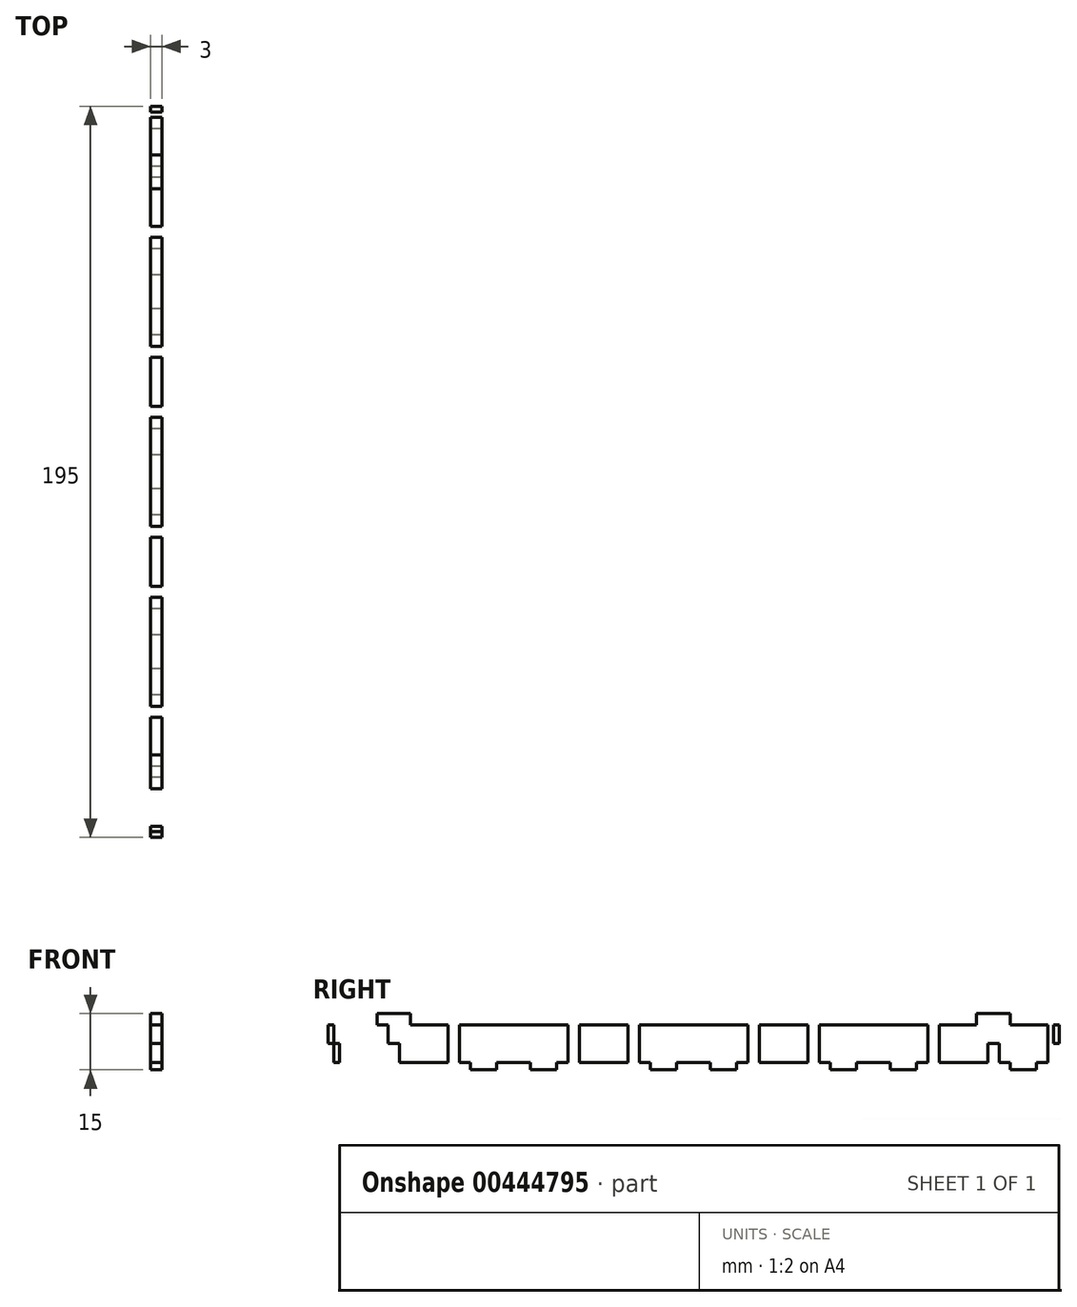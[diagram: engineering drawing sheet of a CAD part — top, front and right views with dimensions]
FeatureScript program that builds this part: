
annotation { "Feature Type Name" : "Feature", "Feature Type Description" : "" }
export const myFeature = defineFeature(function(context is Context, id is Id, definition is map)
    precondition{}
    {
        {
            var Q0;
            Q0=qCreatedBy(makeId("Right.planeOp"),FACE);
            var sketch = newSketch(context, id + "F0", { "sketchPlane" : qUnion([Q0])});
            skLineSegment(sketch, "E0", {"start": v(0, 0) * mm, "end": v(4.5, 0) * mm});
            skLineSegment(sketch, "E1", {"start": v(4.5, 0) * mm, "end": v(4.5, -2) * mm});
            skLineSegment(sketch, "E2", {"start": v(4.5, -2) * mm, "end": v(11.5, -2) * mm});
            skLineSegment(sketch, "E3", {"start": v(11.5, -2) * mm, "end": v(11.5, 0) * mm});
            skLineSegment(sketch, "E4", {"start": v(11.5, 0) * mm, "end": v(36.5, 0) * mm});
            skLineSegment(sketch, "E5", {"start": v(36.5, 0) * mm, "end": v(36.5, -2) * mm});
            skLineSegment(sketch, "E6", {"start": v(36.5, -2) * mm, "end": v(43.5, -2) * mm});
            skLineSegment(sketch, "E7", {"start": v(43.5, -2) * mm, "end": v(43.5, 0) * mm});
            skLineSegment(sketch, "E8", {"start": v(43.5, 0) * mm, "end": v(48, 0) * mm});
            skLineSegment(sketch, "E9.1.0.0", {"start": v(52.5, -2) * mm, "end": v(59.5, -2) * mm});
            skLineSegment(sketch, "E9.1.0.1", {"start": v(59.5, 0) * mm, "end": v(84.5, 0) * mm});
            skLineSegment(sketch, "E9.1.0.2", {"start": v(84.5, -2) * mm, "end": v(91.5, -2) * mm});
            skLineSegment(sketch, "E9.1.0.3", {"start": v(91.5, 0) * mm, "end": v(96, 0) * mm});
            skLineSegment(sketch, "E9.1.0.4", {"start": v(48, 0) * mm, "end": v(52.5, 0) * mm});
            skLineSegment(sketch, "E9.1.0.5", {"start": v(52.5, 0) * mm, "end": v(52.5, -2) * mm});
            skLineSegment(sketch, "E9.1.0.6", {"start": v(91.5, -2) * mm, "end": v(91.5, 0) * mm});
            skLineSegment(sketch, "E9.1.0.7", {"start": v(59.5, -2) * mm, "end": v(59.5, 0) * mm});
            skLineSegment(sketch, "E9.1.0.8", {"start": v(84.5, 0) * mm, "end": v(84.5, -2) * mm});
            skLineSegment(sketch, "E9.2.0.0", {"start": v(100.5, -2) * mm, "end": v(107.5, -2) * mm});
            skLineSegment(sketch, "E9.2.0.1", {"start": v(107.5, 0) * mm, "end": v(132.5, 0) * mm});
            skLineSegment(sketch, "E9.2.0.2", {"start": v(132.5, -2) * mm, "end": v(139.5, -2) * mm});
            skLineSegment(sketch, "E9.2.0.3", {"start": v(139.5, 0) * mm, "end": v(144, 0) * mm});
            skLineSegment(sketch, "E9.2.0.4", {"start": v(96, 0) * mm, "end": v(100.5, 0) * mm});
            skLineSegment(sketch, "E9.2.0.5", {"start": v(100.5, 0) * mm, "end": v(100.5, -2) * mm});
            skLineSegment(sketch, "E9.2.0.6", {"start": v(139.5, -2) * mm, "end": v(139.5, 0) * mm});
            skLineSegment(sketch, "E9.2.0.7", {"start": v(107.5, -2) * mm, "end": v(107.5, 0) * mm});
            skLineSegment(sketch, "E9.2.0.8", {"start": v(132.5, 0) * mm, "end": v(132.5, -2) * mm});
            skLineSegment(sketch, "E9.3.0.0", {"start": v(148.5, -2) * mm, "end": v(155.5, -2) * mm});
            skLineSegment(sketch, "E9.3.0.1", {"start": v(155.5, 0) * mm, "end": v(180.5, 0) * mm});
            skLineSegment(sketch, "E9.3.0.2", {"start": v(180.5, -2) * mm, "end": v(187.5, -2) * mm});
            skLineSegment(sketch, "E9.3.0.3", {"start": v(187.5, 0) * mm, "end": v(192, 0) * mm});
            skLineSegment(sketch, "E9.3.0.4", {"start": v(144, 0) * mm, "end": v(148.5, 0) * mm});
            skLineSegment(sketch, "E9.3.0.5", {"start": v(148.5, 0) * mm, "end": v(148.5, -2) * mm});
            skLineSegment(sketch, "E9.3.0.6", {"start": v(187.5, -2) * mm, "end": v(187.5, 0) * mm});
            skLineSegment(sketch, "E9.3.0.7", {"start": v(155.5, -2) * mm, "end": v(155.5, 0) * mm});
            skLineSegment(sketch, "E9.3.0.8", {"start": v(180.5, 0) * mm, "end": v(180.5, -2) * mm});
            skLineSegment(sketch, "E9.direction1", {"start": v(0, 0) * mm, "end": v(48, 0) * mm, "construction": true});
            skLineSegment(sketch, "E10", {"start": v(0, 0) * mm, "end": v(0, 10) * mm});
            skLineSegment(sketch, "E11", {"start": v(192, 0) * mm, "end": v(192, 10) * mm});
            skLineSegment(sketch, "E12", {"start": v(192, 10) * mm, "end": v(0, 10) * mm});
            skPoint(sketch, "E13.oppositeSnap0", {"position": v(0, 5) * mm});
            skLineSegment(sketch, "E13.bottom", {"start": v(0, 10) * mm, "end": v(-1.5, 10) * mm});
            skLineSegment(sketch, "E13.top", {"start": v(0, 5) * mm, "end": v(-1.5, 5) * mm});
            skLineSegment(sketch, "E13.left", {"start": v(0, 10) * mm, "end": v(0, 5) * mm});
            skLineSegment(sketch, "E13.right", {"start": v(-1.5, 10) * mm, "end": v(-1.5, 5) * mm});
            skPoint(sketch, "E14.oppositeSnap0", {"position": v(192, 5) * mm});
            skLineSegment(sketch, "E14.bottom", {"start": v(192, 10) * mm, "end": v(193.5, 10) * mm});
            skLineSegment(sketch, "E14.top", {"start": v(192, 5) * mm, "end": v(193.5, 5) * mm});
            skLineSegment(sketch, "E14.left", {"start": v(192, 10) * mm, "end": v(192, 5) * mm});
            skLineSegment(sketch, "E14.right", {"start": v(193.5, 10) * mm, "end": v(193.5, 5) * mm});
            skLineSegment(sketch, "E15.bottom", {"start": v(14.5, 10) * mm, "end": v(17.5, 10) * mm});
            skLineSegment(sketch, "E15.top", {"start": v(14.5, 5) * mm, "end": v(17.5, 5) * mm});
            skLineSegment(sketch, "E15.left", {"start": v(14.5, 10) * mm, "end": v(14.5, 5) * mm});
            skLineSegment(sketch, "E15.right", {"start": v(17.5, 10) * mm, "end": v(17.5, 5) * mm});
            skLineSegment(sketch, "E16.bottom", {"start": v(33.5, 10) * mm, "end": v(30.5, 10) * mm});
            skLineSegment(sketch, "E16.top", {"start": v(33.5, 5) * mm, "end": v(30.5, 5) * mm});
            skLineSegment(sketch, "E16.left", {"start": v(33.5, 10) * mm, "end": v(33.5, 5) * mm});
            skLineSegment(sketch, "E16.right", {"start": v(30.5, 10) * mm, "end": v(30.5, 5) * mm});
            skLineSegment(sketch, "E17.bottom", {"start": v(62.5, 10) * mm, "end": v(65.5, 10) * mm});
            skLineSegment(sketch, "E17.top", {"start": v(62.5, 5) * mm, "end": v(65.5, 5) * mm});
            skLineSegment(sketch, "E17.left", {"start": v(62.5, 10) * mm, "end": v(62.5, 5) * mm});
            skLineSegment(sketch, "E17.right", {"start": v(65.5, 10) * mm, "end": v(65.5, 5) * mm});
            skLineSegment(sketch, "E18.bottom", {"start": v(78.5, 10) * mm, "end": v(81.5, 10) * mm});
            skLineSegment(sketch, "E18.top", {"start": v(78.5, 5) * mm, "end": v(81.5, 5) * mm});
            skLineSegment(sketch, "E18.left", {"start": v(78.5, 10) * mm, "end": v(78.5, 5) * mm});
            skLineSegment(sketch, "E18.right", {"start": v(81.5, 10) * mm, "end": v(81.5, 5) * mm});
            skLineSegment(sketch, "E19.bottom", {"start": v(110.5, 10) * mm, "end": v(113.5, 10) * mm});
            skLineSegment(sketch, "E19.top", {"start": v(110.5, 5) * mm, "end": v(113.5, 5) * mm});
            skLineSegment(sketch, "E19.left", {"start": v(110.5, 10) * mm, "end": v(110.5, 5) * mm});
            skLineSegment(sketch, "E19.right", {"start": v(113.5, 10) * mm, "end": v(113.5, 5) * mm});
            skLineSegment(sketch, "E20.bottom", {"start": v(129.5, 10) * mm, "end": v(126.5, 10) * mm});
            skLineSegment(sketch, "E20.top", {"start": v(129.5, 5) * mm, "end": v(126.5, 5) * mm});
            skLineSegment(sketch, "E20.left", {"start": v(129.5, 10) * mm, "end": v(129.5, 5) * mm});
            skLineSegment(sketch, "E20.right", {"start": v(126.5, 10) * mm, "end": v(126.5, 5) * mm});
            skLineSegment(sketch, "E21.bottom", {"start": v(158.5, 10) * mm, "end": v(161.5, 10) * mm});
            skLineSegment(sketch, "E21.top", {"start": v(158.5, 5) * mm, "end": v(161.5, 5) * mm});
            skLineSegment(sketch, "E21.left", {"start": v(158.5, 10) * mm, "end": v(158.5, 5) * mm});
            skLineSegment(sketch, "E21.right", {"start": v(161.5, 10) * mm, "end": v(161.5, 5) * mm});
            skLineSegment(sketch, "E22.bottom", {"start": v(177.5, 10) * mm, "end": v(174.5, 10) * mm});
            skLineSegment(sketch, "E22.top", {"start": v(177.5, 5) * mm, "end": v(174.5, 5) * mm});
            skLineSegment(sketch, "E22.left", {"start": v(177.5, 10) * mm, "end": v(177.5, 5) * mm});
            skLineSegment(sketch, "E22.right", {"start": v(174.5, 10) * mm, "end": v(174.5, 5) * mm});
            skLineSegment(sketch, "E23.top", {"start": v(0, 0) * mm, "end": v(-1.5, 0) * mm});
            skLineSegment(sketch, "E23.left", {"start": v(0, 5) * mm, "end": v(0, 0) * mm});
            skLineSegment(sketch, "E23.right", {"start": v(-1.5, 5) * mm, "end": v(-1.5, 0) * mm});
            skLineSegment(sketch, "E24.top", {"start": v(14.5, 0) * mm, "end": v(17.5, 0) * mm});
            skLineSegment(sketch, "E24.left", {"start": v(14.5, 5) * mm, "end": v(14.5, 0) * mm});
            skLineSegment(sketch, "E24.right", {"start": v(17.5, 5) * mm, "end": v(17.5, 0) * mm});
            skLineSegment(sketch, "E25.bottom", {"start": v(30.5, 5) * mm, "end": v(33.5, 5) * mm});
            skLineSegment(sketch, "E25.top", {"start": v(30.5, 0) * mm, "end": v(33.5, 0) * mm});
            skLineSegment(sketch, "E25.left", {"start": v(30.5, 5) * mm, "end": v(30.5, 0) * mm});
            skLineSegment(sketch, "E25.right", {"start": v(33.5, 5) * mm, "end": v(33.5, 0) * mm});
            skLineSegment(sketch, "E26.top", {"start": v(62.5, 0) * mm, "end": v(65.5, 0) * mm});
            skLineSegment(sketch, "E26.left", {"start": v(62.5, 5) * mm, "end": v(62.5, 0) * mm});
            skLineSegment(sketch, "E26.right", {"start": v(65.5, 5) * mm, "end": v(65.5, 0) * mm});
            skLineSegment(sketch, "E27.top", {"start": v(78.5, 0) * mm, "end": v(81.5, 0) * mm});
            skLineSegment(sketch, "E27.left", {"start": v(78.5, 5) * mm, "end": v(78.5, 0) * mm});
            skLineSegment(sketch, "E27.right", {"start": v(81.5, 5) * mm, "end": v(81.5, 0) * mm});
            skLineSegment(sketch, "E28.top", {"start": v(110.5, 0) * mm, "end": v(113.5, 0) * mm});
            skLineSegment(sketch, "E28.left", {"start": v(110.5, 5) * mm, "end": v(110.5, 0) * mm});
            skLineSegment(sketch, "E28.right", {"start": v(113.5, 5) * mm, "end": v(113.5, 0) * mm});
            skLineSegment(sketch, "E29.bottom", {"start": v(126.5, 5) * mm, "end": v(129.5, 5) * mm});
            skLineSegment(sketch, "E29.top", {"start": v(126.5, 0) * mm, "end": v(129.5, 0) * mm});
            skLineSegment(sketch, "E29.left", {"start": v(126.5, 5) * mm, "end": v(126.5, 0) * mm});
            skLineSegment(sketch, "E29.right", {"start": v(129.5, 5) * mm, "end": v(129.5, 0) * mm});
            skLineSegment(sketch, "E30.top", {"start": v(158.5, 0) * mm, "end": v(161.5, 0) * mm});
            skLineSegment(sketch, "E30.left", {"start": v(158.5, 5) * mm, "end": v(158.5, 0) * mm});
            skLineSegment(sketch, "E30.right", {"start": v(161.5, 5) * mm, "end": v(161.5, 0) * mm});
            skLineSegment(sketch, "E31.bottom", {"start": v(174.5, 5) * mm, "end": v(177.5, 5) * mm});
            skLineSegment(sketch, "E31.top", {"start": v(174.5, 0) * mm, "end": v(177.5, 0) * mm});
            skLineSegment(sketch, "E31.left", {"start": v(174.5, 5) * mm, "end": v(174.5, 0) * mm});
            skLineSegment(sketch, "E31.right", {"start": v(177.5, 5) * mm, "end": v(177.5, 0) * mm});
            skLineSegment(sketch, "E32.top", {"start": v(192, 0) * mm, "end": v(193.5, 0) * mm});
            skLineSegment(sketch, "E32.left", {"start": v(192, 5) * mm, "end": v(192, 0) * mm});
            skLineSegment(sketch, "E32.right", {"start": v(193.5, 5) * mm, "end": v(193.5, 0) * mm});
            skLineSegment(sketch, "E33.bottom", {"start": v(0, 10) * mm, "end": v(1.5, 10) * mm});
            skLineSegment(sketch, "E33.top", {"start": v(0, 5) * mm, "end": v(1.5, 5) * mm});
            skLineSegment(sketch, "E33.right", {"start": v(1.5, 10) * mm, "end": v(1.5, 5) * mm});
            skLineSegment(sketch, "E34.top", {"start": v(0, 0) * mm, "end": v(1.5, 0) * mm});
            skLineSegment(sketch, "E34.right", {"start": v(1.5, 5) * mm, "end": v(1.5, 0) * mm});
            skLineSegment(sketch, "E35.bottom", {"start": v(192, 10) * mm, "end": v(190.5, 10) * mm});
            skLineSegment(sketch, "E35.top", {"start": v(192, 5) * mm, "end": v(190.5, 5) * mm});
            skLineSegment(sketch, "E35.right", {"start": v(190.5, 10) * mm, "end": v(190.5, 5) * mm});
            skLineSegment(sketch, "E36.bottom", {"start": v(190.5, 5) * mm, "end": v(192, 5) * mm});
            skLineSegment(sketch, "E36.top", {"start": v(190.5, 0) * mm, "end": v(192, 0) * mm});
            skLineSegment(sketch, "E36.left", {"start": v(190.5, 5) * mm, "end": v(190.5, 0) * mm});
            skLineSegment(sketch, "E37.bottom", {"start": v(11.5, 10) * mm, "end": v(20.5, 10) * mm});
            skLineSegment(sketch, "E37.top", {"start": v(11.5, 13) * mm, "end": v(20.5, 13) * mm});
            skLineSegment(sketch, "E37.left", {"start": v(11.5, 10) * mm, "end": v(11.5, 13) * mm});
            skLineSegment(sketch, "E37.right", {"start": v(20.5, 10) * mm, "end": v(20.5, 13) * mm});
            skLineSegment(sketch, "E38.bottom", {"start": v(171.5, 10) * mm, "end": v(180.5, 10) * mm});
            skLineSegment(sketch, "E38.top", {"start": v(171.5, 13) * mm, "end": v(180.5, 13) * mm});
            skLineSegment(sketch, "E38.left", {"start": v(171.5, 10) * mm, "end": v(171.5, 13) * mm});
            skLineSegment(sketch, "E38.right", {"start": v(180.5, 10) * mm, "end": v(180.5, 13) * mm});
            skSolve(sketch);
        }
        {
            var Q0;
            Q0=makeQuery(id+"F0.imprint","IMPRINT",FACE,{"disambiguationData":[TD([[makeQuery(id+"F0.imprint","IMPRINT",EDGE,{"derivedFrom":sQuery(id+"F0.wireOp",EDGE,"E0")}),1.0]])]});
            var Q1;
            Q1=makeQuery(id+"F0.imprint","IMPRINT",FACE,{"disambiguationData":[TD([[makeQuery(id+"F0.imprint","IMPRINT",EDGE,{"derivedFrom":sQuery(id+"F0.wireOp",EDGE,"E15.bottom")}),-1.0]])]});
            var Q2;
            {var subQ1=sQuery(id+"F0.wireOp",EDGE,"E15.right");Q2=makeQuery(id+"F0.imprint","IMPRINT",FACE,{"disambiguationData":[TD([[makeQuery(id+"F0.imprint","IMPRINT",EDGE,{"derivedFrom":subQ1}),1.0]])]});}
            var Q3;
            Q3=makeQuery(id+"F0.imprint","IMPRINT",FACE,{"disambiguationData":[TD([[makeQuery(id+"F0.imprint","IMPRINT",EDGE,{"derivedFrom":sQuery(id+"F0.wireOp",EDGE,"E16.bottom")}),1.0]])]});
            var Q4;
            {var subQ4=sQuery(id+"F0.wireOp",EDGE,"E5");Q4=makeQuery(id+"F0.imprint","IMPRINT",FACE,{"disambiguationData":[TD([[makeQuery(id+"F0.imprint","IMPRINT",EDGE,{"derivedFrom":subQ4}),1.0]])]});}
            var Q5;
            Q5=makeQuery(id+"F0.imprint","IMPRINT",FACE,{"disambiguationData":[TD([[makeQuery(id+"F0.imprint","IMPRINT",EDGE,{"derivedFrom":sQuery(id+"F0.wireOp",EDGE,"E17.bottom")}),-1.0]])]});
            var Q6;
            {var subQ0=sQuery(id+"F0.wireOp",EDGE,"E17.right");Q6=makeQuery(id+"F0.imprint","IMPRINT",FACE,{"disambiguationData":[TD([[makeQuery(id+"F0.imprint","IMPRINT",EDGE,{"derivedFrom":subQ0}),1.0]])]});}
            var Q7;
            Q7=makeQuery(id+"F0.imprint","IMPRINT",FACE,{"disambiguationData":[TD([[makeQuery(id+"F0.imprint","IMPRINT",EDGE,{"derivedFrom":sQuery(id+"F0.wireOp",EDGE,"E18.bottom")}),-1.0]])]});
            var Q8;
            Q8=makeQuery(id+"F0.imprint","IMPRINT",FACE,{"disambiguationData":[TD([[makeQuery(id+"F0.imprint","IMPRINT",EDGE,{"derivedFrom":sQuery(id+"F0.wireOp",EDGE,"E9.1.0.2")}),1.0]])]});
            var Q9;
            Q9=makeQuery(id+"F0.imprint","IMPRINT",FACE,{"disambiguationData":[TD([[makeQuery(id+"F0.imprint","IMPRINT",EDGE,{"derivedFrom":sQuery(id+"F0.wireOp",EDGE,"E19.bottom")}),-1.0]])]});
            var Q10;
            {var subQ2=sQuery(id+"F0.wireOp",EDGE,"E19.right");Q10=makeQuery(id+"F0.imprint","IMPRINT",FACE,{"disambiguationData":[TD([[makeQuery(id+"F0.imprint","IMPRINT",EDGE,{"derivedFrom":subQ2}),1.0]])]});}
            var Q11;
            Q11=makeQuery(id+"F0.imprint","IMPRINT",FACE,{"disambiguationData":[TD([[makeQuery(id+"F0.imprint","IMPRINT",EDGE,{"derivedFrom":sQuery(id+"F0.wireOp",EDGE,"E20.bottom")}),1.0]])]});
            var Q12;
            Q12=makeQuery(id+"F0.imprint","IMPRINT",FACE,{"disambiguationData":[TD([[makeQuery(id+"F0.imprint","IMPRINT",EDGE,{"derivedFrom":sQuery(id+"F0.wireOp",EDGE,"E9.2.0.2")}),1.0]])]});
            var Q13;
            Q13=makeQuery(id+"F0.imprint","IMPRINT",FACE,{"disambiguationData":[TD([[makeQuery(id+"F0.imprint","IMPRINT",EDGE,{"derivedFrom":sQuery(id+"F0.wireOp",EDGE,"E21.bottom")}),-1.0]])]});
            var Q14;
            {var subQ1=sQuery(id+"F0.wireOp",EDGE,"E21.right");Q14=makeQuery(id+"F0.imprint","IMPRINT",FACE,{"disambiguationData":[TD([[makeQuery(id+"F0.imprint","IMPRINT",EDGE,{"derivedFrom":subQ1}),1.0]])]});}
            var Q15;
            Q15=makeQuery(id+"F0.imprint","IMPRINT",FACE,{"disambiguationData":[TD([[makeQuery(id+"F0.imprint","IMPRINT",EDGE,{"derivedFrom":sQuery(id+"F0.wireOp",EDGE,"E22.bottom")}),1.0]])]});
            var Q16;
            Q16=makeQuery(id+"F0.imprint","IMPRINT",FACE,{"disambiguationData":[TD([[makeQuery(id+"F0.imprint","IMPRINT",EDGE,{"derivedFrom":sQuery(id+"F0.wireOp",EDGE,"E9.3.0.2")}),1.0]])]});
            var Q17;
            Q17=makeQuery(id+"F0.imprint","IMPRINT",FACE,{"disambiguationData":[TD([[makeQuery(id+"F0.imprint","IMPRINT",EDGE,{"derivedFrom":sQuery(id+"F0.wireOp",EDGE,"E33.bottom")}),-1.0]])]});
            var Q18;
            Q18=makeQuery(id+"F0.imprint","IMPRINT",FACE,{"disambiguationData":[TD([[makeQuery(id+"F0.imprint","IMPRINT",EDGE,{"derivedFrom":sQuery(id+"F0.wireOp",EDGE,"E35.bottom")}),1.0]])]});
            var Q19;
            Q19=makeQuery(id+"F0.imprint","IMPRINT",FACE,{"disambiguationData":[TD([[makeQuery(id+"F0.imprint","IMPRINT",EDGE,{"derivedFrom":sQuery(id+"F0.wireOp",EDGE,"E14.bottom")}),-1.0]])]});
            var Q20;
            Q20=makeQuery(id+"F0.imprint","IMPRINT",FACE,{"disambiguationData":[TD([[makeQuery(id+"F0.imprint","IMPRINT",EDGE,{"derivedFrom":sQuery(id+"F0.wireOp",EDGE,"E13.bottom")}),1.0]])]});
            var Q21;
            {var subQ0=sQuery(id+"F0.wireOp",EDGE,"E22.left");Q21=makeQuery(id+"F0.imprint","IMPRINT",FACE,{"disambiguationData":[TD([[makeQuery(id+"F0.imprint","IMPRINT",EDGE,{"derivedFrom":subQ0}),-1.0]])]});}
            var Q22;
            Q22=makeQuery(id+"F0.imprint","IMPRINT",FACE,{"disambiguationData":[TD([[makeQuery(id+"F0.imprint","IMPRINT",EDGE,{"derivedFrom":sQuery(id+"F0.wireOp",EDGE,"E38.top")}),-1.0]])]});
            var Q23;
            {var subQ0=sQuery(id+"F0.wireOp",EDGE,"E15.left");Q23=makeQuery(id+"F0.imprint","IMPRINT",FACE,{"disambiguationData":[TD([[makeQuery(id+"F0.imprint","IMPRINT",EDGE,{"derivedFrom":subQ0}),1.0]])]});}
            var Q24;
            Q24=makeQuery(id+"F0.imprint","IMPRINT",FACE,{"disambiguationData":[TD([[makeQuery(id+"F0.imprint","IMPRINT",EDGE,{"derivedFrom":sQuery(id+"F0.wireOp",EDGE,"E37.top")}),-1.0]])]});
            extrude(context, id + "F1", {"entities" : qUnion([Q0, Q1, Q2, Q3, Q4, Q5, Q6, Q7, Q8, Q9, Q10, Q11, Q12, Q13, Q14, Q15, Q16, Q17, Q18, Q19, Q20, Q21, Q22, Q23, Q24]), "depth" : 3 * mm});
        }
    });
